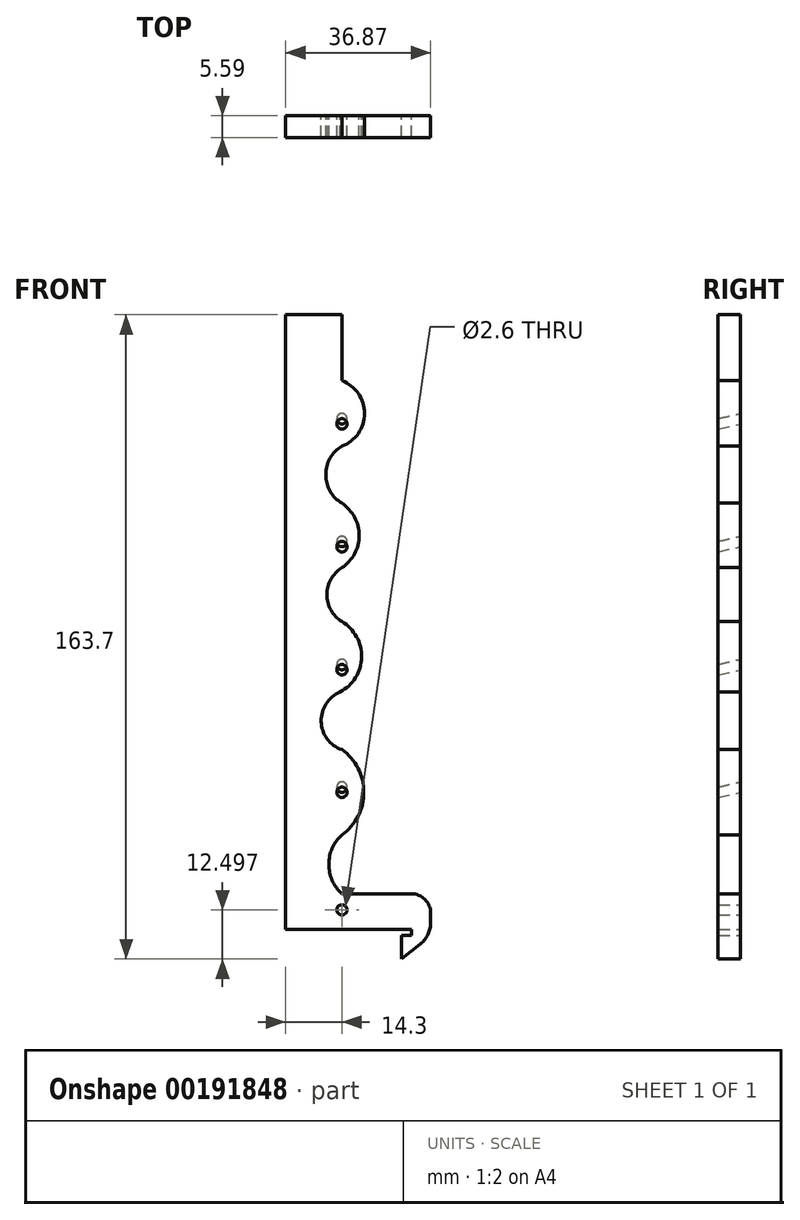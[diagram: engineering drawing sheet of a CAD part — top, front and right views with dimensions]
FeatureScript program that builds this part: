
annotation { "Feature Type Name" : "Feature", "Feature Type Description" : "" }
export const myFeature = defineFeature(function(context is Context, id is Id, definition is map)
    precondition{}
    {
        {
            var Q0;
            Q0=qCreatedBy(makeId("Front.planeOp"),FACE);
            var sketch = newSketch(context, id + "F0", { "sketchPlane" : qUnion([Q0])});
            skLineSegment(sketch, "E0", {"start": v(-14.3, 105.93) * mm, "end": v(-14.3, -50.27) * mm});
            skLineSegment(sketch, "E1", {"start": v(15.2, -51.77) * mm, "end": v(17.7, -51.77) * mm});
            skLineSegment(sketch, "E2", {"start": v(-14.3, -50.27) * mm, "end": v(17.7, -50.27) * mm});
            skLineSegment(sketch, "E3", {"start": v(17.7, -51.77) * mm, "end": v(17.7, -50.27) * mm});
            skLineSegment(sketch, "E4", {"start": v(15.2, -51.77) * mm, "end": v(15.2, -57.77) * mm});
            skLineSegment(sketch, "E5", {"start": v(15.2, -57.77) * mm, "end": v(22.57, -51.77) * mm});
            skLineSegment(sketch, "E6", {"start": v(22.57, -51.77) * mm, "end": v(22.57, -41.17) * mm});
            skLineSegment(sketch, "E7", {"start": v(22.57, -41.17) * mm, "end": v(0, -41.17) * mm});
            skArc(sketch, "E8", {"start": v(-0.45, 10.07) * mm, "mid": v(-5.25, 2.6) * mm, "end": v(0, -4.55) * mm});
            skArc(sketch, "E9", {"start": v(0, -26.24) * mm, "mid": v(5.56, -15.4) * mm, "end": v(0, -4.55) * mm});
            skArc(sketch, "E10", {"start": v(0, -26.24) * mm, "mid": v(-3.32, -33.7) * mm, "end": v(0, -41.17) * mm});
            skLineSegment(sketch, "E11", {"start": v(-29.5, -45.27) * mm, "end": v(32.43, -45.27) * mm, "construction": true});
            skPoint(sketch, "E12", {"position": v(0, -45.27) * mm});
            skLineSegment(sketch, "E13", {"start": v(-27.66, -14.07) * mm, "end": v(25.15, -14.07) * mm, "construction": true});
            skLineSegment(sketch, "E14", {"start": v(0, 17.13) * mm, "end": v(0, -51.45) * mm, "construction": true});
            skLineSegment(sketch, "E15", {"start": v(0, -51.45) * mm, "end": v(0, 89.16) * mm, "construction": true});
            skLineSegment(sketch, "E16", {"start": v(-27.86, 17.13) * mm, "end": v(33, 17.13) * mm, "construction": true});
            skLineSegment(sketch, "E17", {"start": v(-14.3, 105.93) * mm, "end": v(0, 105.93) * mm});
            skLineSegment(sketch, "E18", {"start": v(0, 105.93) * mm, "end": v(0, 89.16) * mm});
            skLineSegment(sketch, "E19", {"start": v(-32.14, 48.33) * mm, "end": v(32.87, 48.33) * mm, "construction": true});
            skLineSegment(sketch, "E20", {"start": v(-31.94, 79.53) * mm, "end": v(34.48, 79.53) * mm, "construction": true});
            skArc(sketch, "E21", {"start": v(-0.45, 10.07) * mm, "mid": v(5.01, 18.9) * mm, "end": v(0, 27.99) * mm});
            skArc(sketch, "E22", {"start": v(0, 41.66) * mm, "mid": v(-3.8, 34.82) * mm, "end": v(0, 27.99) * mm});
            skArc(sketch, "E23", {"start": v(0, 41.66) * mm, "mid": v(4.39, 49.85) * mm, "end": v(0, 58.04) * mm});
            skArc(sketch, "E24", {"start": v(0, 72.56) * mm, "mid": v(-4.1, 65.3) * mm, "end": v(0, 58.04) * mm});
            skArc(sketch, "E25", {"start": v(0, 72.56) * mm, "mid": v(5.76, 80.86) * mm, "end": v(0, 89.16) * mm});
            skCircle(sketch, "E26", {"center": v(0, -45.27) * mm, "radius": 1.3 * mm});
            skSolve(sketch);
        }
        {
            var Q0;
            Q0=sQuery(id+"F0.wireOp",EDGE,"E13");
            cPlane(context, id + "F1", {"entities" : qUnion([Q0]), "cplaneType" : CPlaneType.LINE_ANGLE, "offset" : 25 * mm, "angle" : 13.27 * degree, "width" : 150 * mm, "height" : 150 * mm});
        }
        {
            var Q0;
            Q0=sQuery(id+"F0.wireOp",EDGE,"E16");
            cPlane(context, id + "F2", {"entities" : qUnion([Q0]), "cplaneType" : CPlaneType.LINE_ANGLE, "offset" : 25 * mm, "angle" : 13.27 * degree, "width" : 150 * mm, "height" : 150 * mm});
        }
        {
            var Q0;
            Q0=qCreatedBy(id+"F1.planeOp",FACE);
            var sketch = newSketch(context, id + "F3", { "sketchPlane" : qUnion([Q0])});
            skCircle(sketch, "E27", {"center": v(0, -13.71) * mm, "radius": 1.3 * mm});
            skSolve(sketch);
        }
        {
            var Q0;
            Q0=qCreatedBy(id+"F2.planeOp",FACE);
            var sketch = newSketch(context, id + "F4", { "sketchPlane" : qUnion([Q0])});
            skCircle(sketch, "E28", {"center": v(0, 16.6) * mm, "radius": 1.3 * mm});
            skSolve(sketch);
        }
        {
            var Q0;
            Q0=sQuery(id+"F0.wireOp",EDGE,"E19");
            cPlane(context, id + "F5", {"entities" : qUnion([Q0]), "cplaneType" : CPlaneType.LINE_ANGLE, "offset" : 25 * mm, "angle" : 13.27 * degree, "width" : 150 * mm, "height" : 150 * mm});
        }
        {
            var Q0;
            Q0=sQuery(id+"F0.wireOp",EDGE,"E20");
            cPlane(context, id + "F6", {"entities" : qUnion([Q0]), "cplaneType" : CPlaneType.LINE_ANGLE, "offset" : 25 * mm, "angle" : 13.27 * degree, "width" : 150 * mm, "height" : 150 * mm});
        }
        {
            var Q0;
            Q0=qCreatedBy(id+"F5.planeOp",FACE);
            var sketch = newSketch(context, id + "F7", { "sketchPlane" : qUnion([Q0])});
            skCircle(sketch, "E29", {"center": v(0, 47.04) * mm, "radius": 1.3 * mm});
            skSolve(sketch);
        }
        {
            var Q0;
            Q0=qCreatedBy(id+"F6.planeOp",FACE);
            var sketch = newSketch(context, id + "F8", { "sketchPlane" : qUnion([Q0])});
            skCircle(sketch, "E30", {"center": v(0, 77.4) * mm, "radius": 1.3 * mm});
            skSolve(sketch);
        }
        {
            var Q0;
            Q0=makeQuery(id+"F0.imprint","IMPRINT",FACE,{"disambiguationData":[TD([[makeQuery(id+"F0.imprint","IMPRINT",EDGE,{"derivedFrom":sQuery(id+"F0.wireOp",EDGE,"E0")}),1.0]])]});
            extrude(context, id + "F9", {"entities" : qUnion([Q0]), "depth" : 5.6 * mm});
        }
        {
            var Q0;
            Q0 = qSketchRegion(id + "F3", true);
            var Q1;
            Q1 = qSketchRegion(id + "F7", true);
            var Q2;
            Q2 = qSketchRegion(id + "F8", true);
            var Q3;
            Q3 = qSketchRegion(id + "F4", true);
            extrude(context, id + "F10", {"entities" : qUnion([Q0, Q1, Q2, Q3]), "operationType" : NewBodyOperationType.REMOVE, "endBound" : BoundingType.SYMMETRIC, "oppositeDirection" : true, "depth" : 25 * mm});
        }
        {
            var Q0;
            Q0=makeQuery(id+"F9.opExtrude","SWEPT_EDGE",EDGE,{"disambiguationData":[OSD([sQuery(id+"F0.wireOp",EDGE,"E6"),sQuery(id+"F0.wireOp",EDGE,"E7")])]});
            fillet(context, id + "F11", {"entities" : qUnion([Q0]), "radius" : 5 * mm, "tangentPropagation" : true, "allowEdgeOverflow" : false});
        }
        {
            var Q0;
            Q0=makeQuery(id+"F9.opExtrude","SWEPT_EDGE",EDGE,{"disambiguationData":[OSD([sQuery(id+"F0.wireOp",EDGE,"E5"),sQuery(id+"F0.wireOp",EDGE,"E6")])]});
            fillet(context, id + "F12", {"entities" : qUnion([Q0]), "radius" : 7 * mm, "tangentPropagation" : true, "allowEdgeOverflow" : false});
        }
    });
